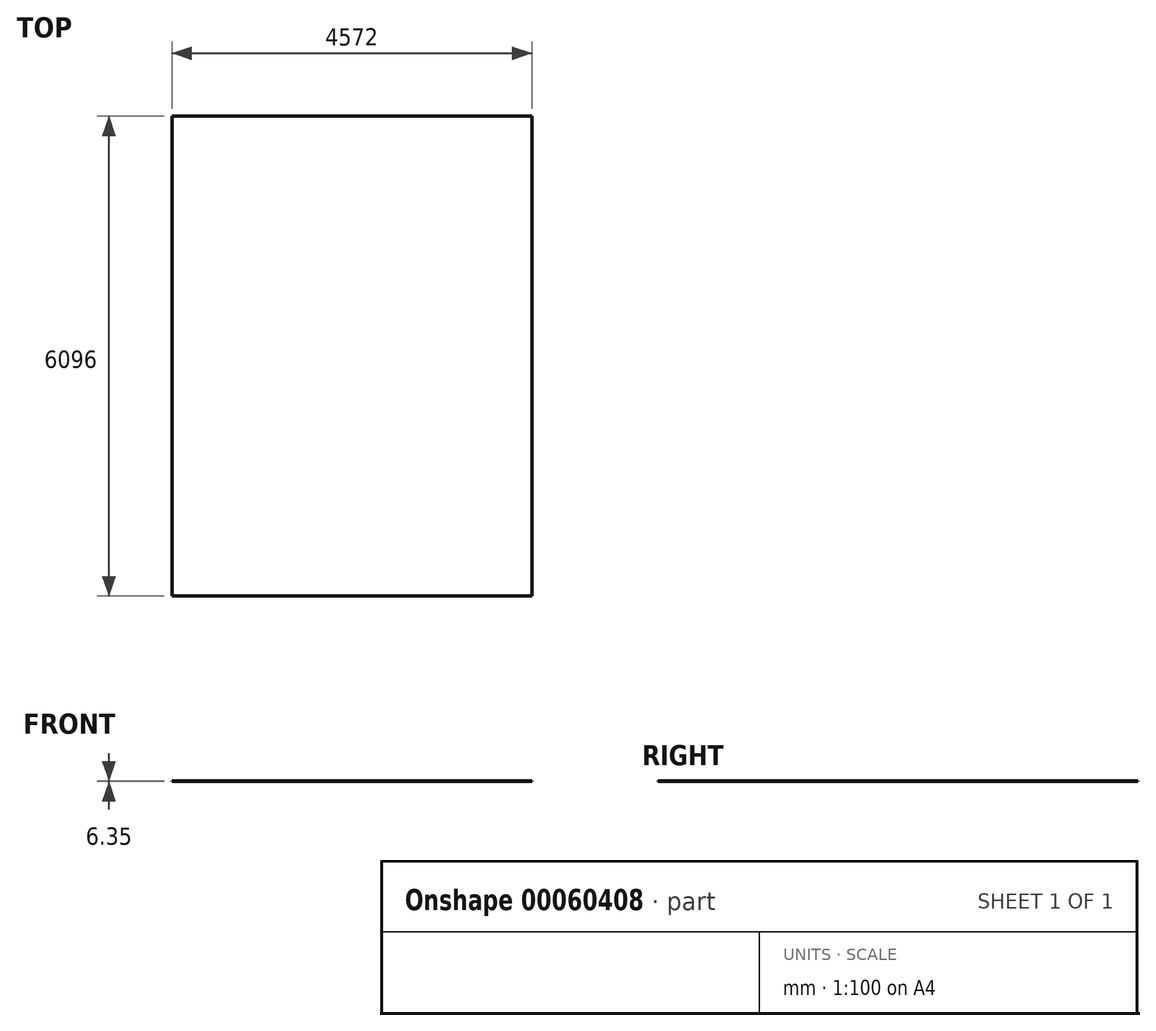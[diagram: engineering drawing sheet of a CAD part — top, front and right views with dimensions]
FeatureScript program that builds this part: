
annotation { "Feature Type Name" : "Feature", "Feature Type Description" : "" }
export const myFeature = defineFeature(function(context is Context, id is Id, definition is map)
    precondition{}
    {
        {
            var Q0;
            Q0=qCreatedBy(makeId("Top.planeOp"),FACE);
            var sketch = newSketch(context, id + "F0", { "sketchPlane" : qUnion([Q0])});
            skLineSegment(sketch, "E0.bottom", {"start": v(0, 5963.57) * mm, "end": v(-4572, 5963.57) * mm});
            skLineSegment(sketch, "E0.top", {"start": v(0, -132.43) * mm, "end": v(-4572, -132.43) * mm});
            skLineSegment(sketch, "E0.left", {"start": v(0, 5963.57) * mm, "end": v(0, -132.43) * mm});
            skLineSegment(sketch, "E0.right", {"start": v(-4572, 5963.57) * mm, "end": v(-4572, -132.43) * mm});
            skSolve(sketch);
        }
        {
            var Q0;
            Q0=makeQuery(id+"F0.imprint","IMPRINT",FACE,{"disambiguationData":[TD([[makeQuery(id+"F0.imprint","IMPRINT",EDGE,{"derivedFrom":sQuery(id+"F0.wireOp",EDGE,"E0.bottom")}),1.0]])]});
            extrude(context, id + "F1", {"entities" : qUnion([Q0]), "depth" : 6.35 * mm});
        }
    });
